# Revit family: JOMA_Balksko kombi_Grundform 500
name_source: partatom
category: Structural Connections
revit_build: Autodesk Revit Structure 2012 (Build: 20110309_2315(x64)
units: mm (PartAtom-declared; Revit-internal decimal feet)

## types (8) — shared parameters
D = 42 mm  [stored 0.137795 ft]
Default Elevation = 1219 mm
E = 47 mm  [stored 0.154199 ft]
F = 85 mm  [stored 0.278871 ft]
Grundform 500 = Yes
Länk Joma Dimensioneringsverktyg = http://www.joma.se
Material = Varmförzinkad stålplåt
Typ = GRUNDFORM 500
Vikt = 0,65
X = 35 mm  [stored 0.114829 ft]
Y = 140 mm  [stored 0.459318 ft]

## per-type parameters (varying)
| type | A | B |
| 5245228  45x228 | 45 mm  [stored 0.147638 ft] | 228 mm  [stored 0.748031 ft] |
| 5251225  51x225 | 51 mm | 225 mm  [stored 0.738189 ft] |
| 5272214  72x214 | 72 mm  [stored 0.23622 ft] | 214 mm  [stored 0.7021 ft] |
| 5210200  100x200 | 100 mm  [stored 0.328084 ft] | 200 mm  [stored 0.656168 ft] |
| 5212190  120x190 | 120 mm  [stored 0.393701 ft] | 190 mm |
| 5214180  140x180 | 140 mm  [stored 0.459318 ft] | 180 mm  [stored 0.590551 ft] |
| 5215190  115x190 | 115 mm  [stored 0.377297 ft] | 192 mm  [stored 0.629921 ft] |
| 5290205 90x205 | 90 mm  [stored 0.295276 ft] | 205 mm  [stored 0.672572 ft] |

note: [stored X ft] marks values corroborated as IEEE doubles in the binary element streams (Revit-internal decimal feet)

## geometry (parser evidence)
native form markers: Sweep x1
no freeform markers — native parametric forms only
